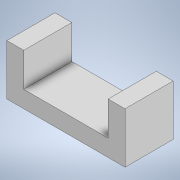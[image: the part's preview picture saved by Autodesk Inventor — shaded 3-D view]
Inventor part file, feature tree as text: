
AUTODESK INVENTOR PART (.ipt)
format: ipt  version: 2021 (Build 250183000, 183)  size: 239,104 bytes
history: native  units: in
note: dims shown in document units (in); Inventor stores cm internally (conversion verified against a paired STEP export)
features: extrude x2, sketch x2
ambient origin geometry x8: Origin, YZ Plane, XZ Plane, XY Plane, X Axis, Y Axis, Z Axis, Center Point
bodies: Solid1 (feature_tree)
feature tree (4):
  extrude  "Extrusion1"  Depth=0.2244in
  extrude  "Extrusion2"  Depth=0.0787in
  sketch  "Sketch1"  dims[d0=0.5512in d1=0.2244in]
  sketch  "Sketch2"  dims[d2=0.0787in d3=0.0in d4=0.0787in d5=0.1575in d6=0.0in]
